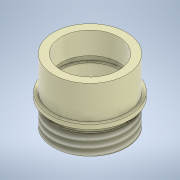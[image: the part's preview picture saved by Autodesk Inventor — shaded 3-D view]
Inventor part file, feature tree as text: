
AUTODESK INVENTOR PART (.ipt)
format: ipt  version: 2020 (Build 240168000, 168)  size: 166,912 bytes
history: native  units: mm
features: revolve x1, thread x1
ambient origin geometry x8: Origin, YZ Plane, XZ Plane, XY Plane, X Axis, Y Axis, Z Axis, Center Point
bodies: Body1 (feature_tree)
feature tree (2):
  revolve  "Revolution1"  [1 undecoded]
  thread  "Thread3"  [1 undecoded]
note: 2 required parameter values undecoded (feature->parameter linkage not recoverable at this tier; creation-order binding heuristic only, values carry confidence <= 0.55)